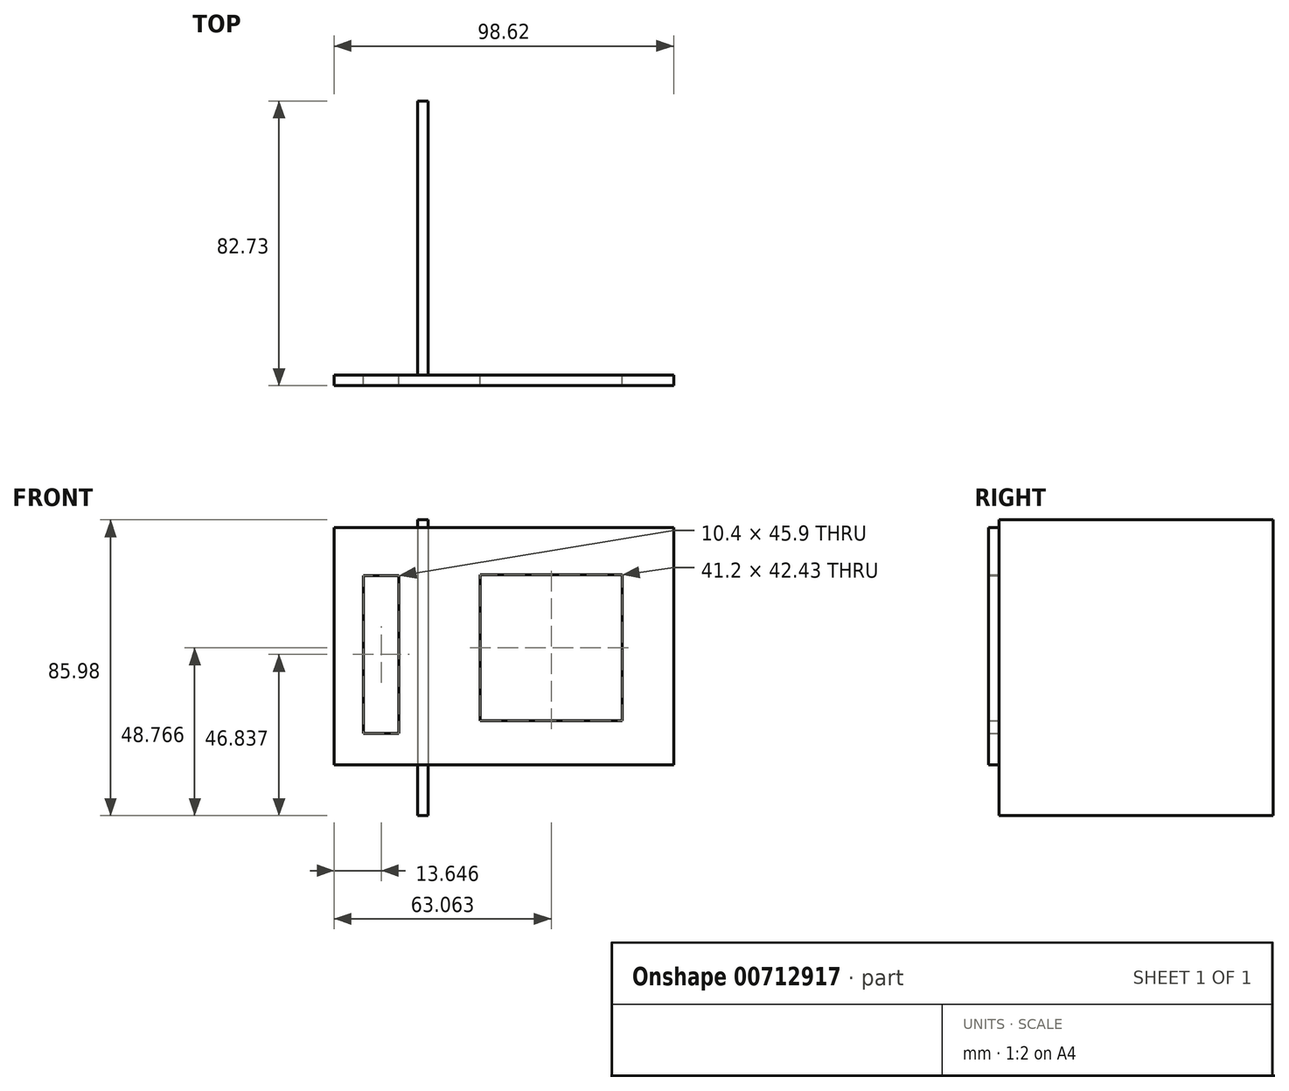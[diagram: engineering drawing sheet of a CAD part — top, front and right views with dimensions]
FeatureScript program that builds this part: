
annotation { "Feature Type Name" : "Feature", "Feature Type Description" : "" }
export const myFeature = defineFeature(function(context is Context, id is Id, definition is map)
    precondition{}
    {
        {
            var Q0;
            Q0=qCreatedBy(makeId("Right.planeOp"),FACE);
            var sketch = newSketch(context, id + "F0", { "sketchPlane" : qUnion([Q0])});
            skLineSegment(sketch, "E0.bottom", {"start": v(-32.22, 36.28) * mm, "end": v(47.51, 36.28) * mm});
            skLineSegment(sketch, "E0.top", {"start": v(-32.22, -49.7) * mm, "end": v(47.51, -49.7) * mm});
            skLineSegment(sketch, "E0.left", {"start": v(-32.22, 36.28) * mm, "end": v(-32.22, -49.7) * mm});
            skLineSegment(sketch, "E0.right", {"start": v(47.51, 36.28) * mm, "end": v(47.51, -49.7) * mm});
            skSolve(sketch);
        }
        {
            var Q0;
            Q0 = qSketchRegion(id + "F0", true);
            extrude(context, id + "F1", {"entities" : qUnion([Q0]), "depth" : 3 * mm, "offsetDistance" : 25 * mm, "symmetric" : true});
        }
        {
            var Q0;
            Q0=makeQuery(id+"F1.opExtrude","SWEPT_FACE",FACE,{"disambiguationData":[OSD([sQuery(id+"F0.wireOp",EDGE,"E0.left")])]});
            var sketch = newSketch(context, id + "F2", { "sketchPlane" : qUnion([Q0])});
            skLineSegment(sketch, "E1.bottom", {"start": v(-25.76, 33.96) * mm, "end": v(72.86, 33.96) * mm});
            skLineSegment(sketch, "E1.top", {"start": v(-25.76, -34.9) * mm, "end": v(72.86, -34.9) * mm});
            skLineSegment(sketch, "E1.left", {"start": v(-25.76, 33.96) * mm, "end": v(-25.76, -34.9) * mm});
            skLineSegment(sketch, "E1.right", {"start": v(72.86, 33.96) * mm, "end": v(72.86, -34.9) * mm});
            skPoint(sketch, "E2", {"position": v(0, 15.36) * mm});
            skPoint(sketch, "E3", {"position": v(0, -20.15) * mm});
            skLineSegment(sketch, "E4.bottom", {"start": v(16.7, 20.28) * mm, "end": v(57.9, 20.28) * mm});
            skLineSegment(sketch, "E4.top", {"start": v(16.7, -22.15) * mm, "end": v(57.9, -22.15) * mm});
            skLineSegment(sketch, "E4.left", {"start": v(16.7, 20.28) * mm, "end": v(16.7, -22.15) * mm});
            skLineSegment(sketch, "E4.right", {"start": v(57.9, 20.28) * mm, "end": v(57.9, -22.15) * mm});
            skLineSegment(sketch, "E5.bottom", {"start": v(-17.31, 20.09) * mm, "end": v(-6.92, 20.09) * mm});
            skLineSegment(sketch, "E5.top", {"start": v(-17.31, -25.81) * mm, "end": v(-6.92, -25.81) * mm});
            skLineSegment(sketch, "E5.left", {"start": v(-17.31, 20.09) * mm, "end": v(-17.31, -25.81) * mm});
            skLineSegment(sketch, "E5.right", {"start": v(-6.92, 20.09) * mm, "end": v(-6.92, -25.81) * mm});
            skSolve(sketch);
        }
        {
            var Q0;
            Q0 = qSketchRegion(id + "F2", true);
            extrude(context, id + "F3", {"entities" : qUnion([Q0]), "depth" : 3 * mm, "offsetDistance" : 25 * mm});
        }
    });
